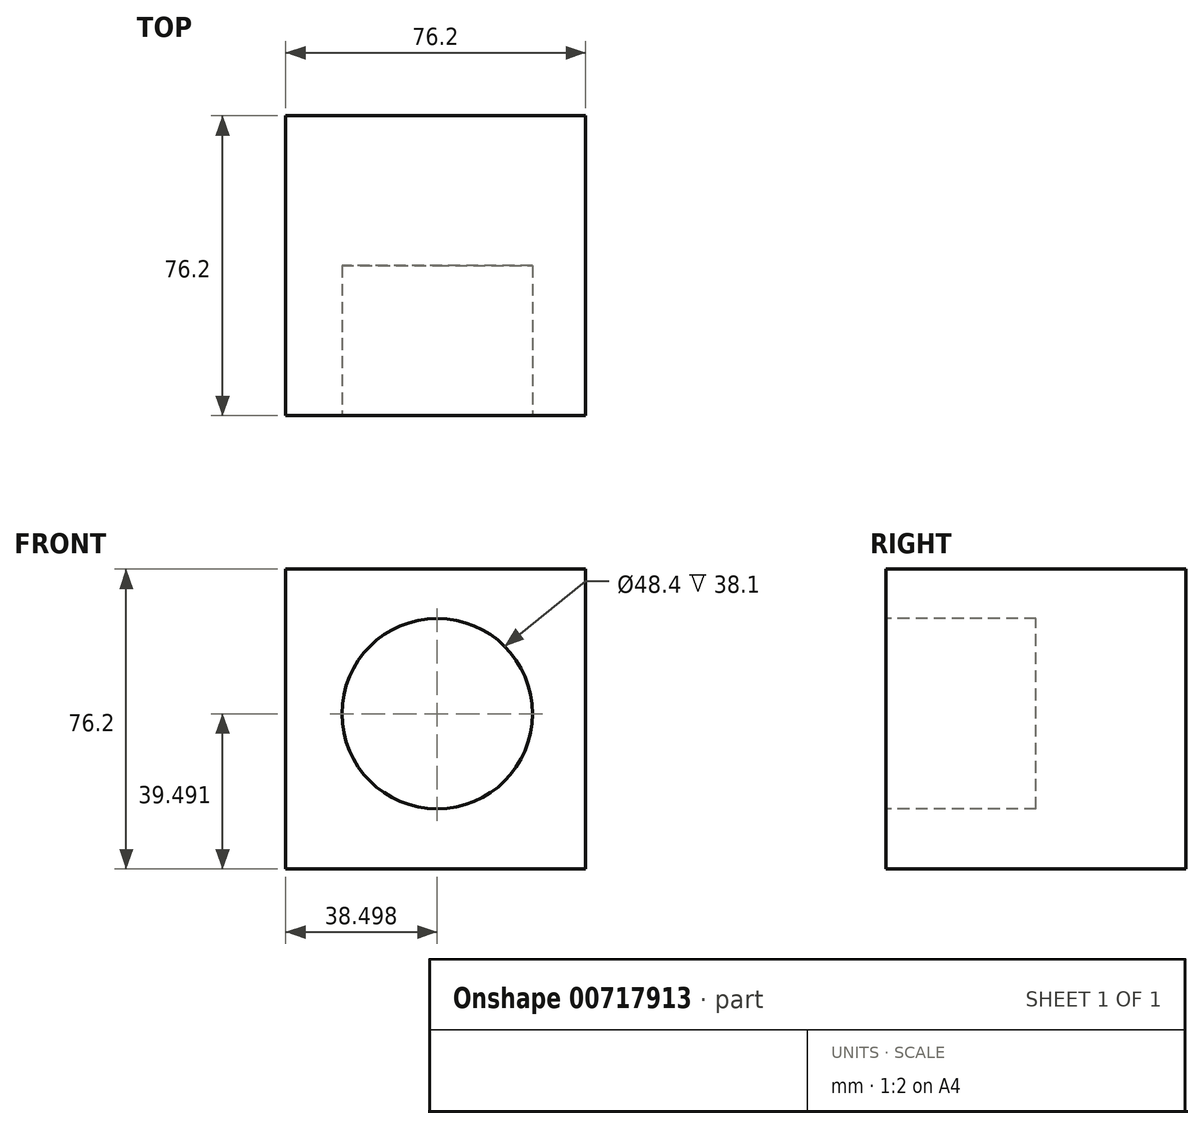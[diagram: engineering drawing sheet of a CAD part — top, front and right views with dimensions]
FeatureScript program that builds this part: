
annotation { "Feature Type Name" : "Feature", "Feature Type Description" : "" }
export const myFeature = defineFeature(function(context is Context, id is Id, definition is map)
    precondition{}
    {
        {
            var Q0;
            Q0=qCreatedBy(makeId("Front.planeOp"),FACE);
            var sketch = newSketch(context, id + "F0", { "sketchPlane" : qUnion([Q0])});
            skLineSegment(sketch, "E0.bottom", {"start": v(-43.29, 42.36) * mm, "end": v(32.91, 42.36) * mm});
            skLineSegment(sketch, "E0.top", {"start": v(-43.29, -33.84) * mm, "end": v(32.91, -33.84) * mm});
            skLineSegment(sketch, "E0.left", {"start": v(-43.29, 42.36) * mm, "end": v(-43.29, -33.84) * mm});
            skLineSegment(sketch, "E0.right", {"start": v(32.91, 42.36) * mm, "end": v(32.91, -33.84) * mm});
            skSolve(sketch);
        }
        {
            var Q0;
            Q0=makeQuery(id+"F0.imprint","IMPRINT",FACE,{"disambiguationData":[TD([[makeQuery(id+"F0.imprint","IMPRINT",EDGE,{"derivedFrom":sQuery(id+"F0.wireOp",EDGE,"E0.bottom")}),-1.0]])]});
            extrude(context, id + "F1", {"entities" : qUnion([Q0]), "depth" : 76.2 * mm, "offsetDistance" : 25.4 * mm});
        }
        {
            var Q0;
            Q0=makeQuery(id+"F1.opExtrude","CAP_FACE",FACE,{"disambiguationData":[OSD([sQuery(id+"F0.wireOp",EDGE,"E0.bottom"),sQuery(id+"F0.wireOp",EDGE,"E0.top"),sQuery(id+"F0.wireOp",EDGE,"E0.left"),sQuery(id+"F0.wireOp",EDGE,"E0.right")])],"isStart":false});
            var sketch = newSketch(context, id + "F2", { "sketchPlane" : qUnion([Q0])});
            skCircle(sketch, "E1", {"center": v(-4.8, 5.65) * mm, "radius": 24.2 * mm});
            skSolve(sketch);
        }
        {
            var Q0;
            Q0=makeQuery(id+"F2.imprint","IMPRINT",FACE,{"disambiguationData":[TD([[makeQuery(id+"F2.imprint","IMPRINT",EDGE,{"derivedFrom":sQuery(id+"F2.wireOp",EDGE,"E1")}),1.0]])]});
            extrude(context, id + "F3", {"entities" : qUnion([Q0]), "operationType" : NewBodyOperationType.REMOVE, "endBound" : BoundingType.SYMMETRIC, "oppositeDirection" : true, "depth" : 76.2 * mm, "offsetDistance" : 25.4 * mm});
        }
    });
